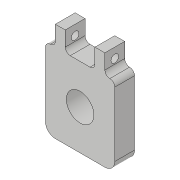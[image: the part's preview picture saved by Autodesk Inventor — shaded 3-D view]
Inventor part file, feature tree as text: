
AUTODESK INVENTOR PART (.ipt)
format: ipt  version: 2018.3 (Build 223284000, 284)  size: 136,192 bytes
history: native  units: in
note: dims shown in document units (in); Inventor stores cm internally (conversion verified against a paired STEP export)
features: extrude x3, sketch x3, fillet x2
ambient origin geometry x8: Origin, YZ Plane, XZ Plane, XY Plane, X Axis, Y Axis, Z Axis, Center Point
bodies: Solid1 (feature_tree)
feature tree (8):
  extrude  "Extrusion1"  Depth=2.0in
  extrude  "Extrusion2"  Depth=0.25in
  extrude  "Extrusion3"  Depth=0.75in
  fillet  "Fillet2"  Radius=0.5in
  fillet  "Fillet3"  Radius=0.755in
  sketch  "Sketch1"  dims[d0=1.75in d1=2.0in]
  sketch  "Sketch2"  dims[d3=0.25in d4=0.25in]
  sketch  "Sketch3"  dims[d5=0.25in d6=0.75in d7=0.5in d8=0.0in d9=0.755in d10=0.695in d11=0.5in d12=0.0in d13=0.1925in d14=0.25in d15=0.25in d16=0.5in d17=0.0in d19=0.25in d20=0.5in d21=0.875in d22=1.0in d23=0.875in d24=0.125in d25=0.25in]
